# Revit family: TowelRail_Single_Abey_Builders_600_FaceBased
name_source: partatom
category: Specialty Equipment
units: mm (PartAtom-declared; Revit-internal decimal feet)

## family parameters
Cut with Voids When Loaded = No
Host = Face
Maintain Annotation Orientation = No
OmniClass Number = 23.31.25.25
OmniClass Title = Towel Bars
Part Type = Normal
Room Calculation Point = No
Round Connector Dimension = Use Diameter
Shared = No

## types (3) — shared parameters
Assembly Code = C1030210
Default Elevation = 900 mm
IfcExportAs = IfcFurniture
IfcExportType = NOTDEFINED
Manufacturer = Abey
ManufacturerOverallDepth = 78 mm
ManufacturerOverallHeight = 55 mm
ManufacturerOverallWidth = 600 mm
ManufacturerURLProductSpecific = https://www.abeyspecifier.com.au
ModifiedIssue = 20251103 $
URL = https://www.abey.com.au
Uniclass2015Code = Pr_40_20_76_90
Uniclass2015Title = Towel rails
Uniclass2015Version = Products v1.38
zero-valued in all types: Cost

## per-type parameters (varying)
| type | Description | ManufacturerSpecCode | Material | Model | Type Comments |
| Chrome (1AB-STR-600) | Abey Builders Single Towel Rail 600mm Chrome | 1AB-STR-600 | Metal_Abey_Chrome | 1AB-STR-600 | Towel Rail - Single - 600 - Chrome |
| Brushed Nickel (1AB-STR-600-BN) | Abey Builders Single Towel Rail 600mm Brushed Nickel | 1AB-STR-600-BN | Metal_Abey_BrushedNickel | 1AB-STR-600-BN | Towel Rail - Single - 600 - Brushed Nickel |
| Black (1AB-STR-600-B) | Abey Builders Single Towel Rail 600mm Black | 1AB-STR-600-B | Metal_Abey_Black | 1AB-STR-600-B | Towel Rail - Single - 600 - Black |

## geometry (parser evidence)
native form markers: Sweep x6
no freeform markers — native parametric forms only
